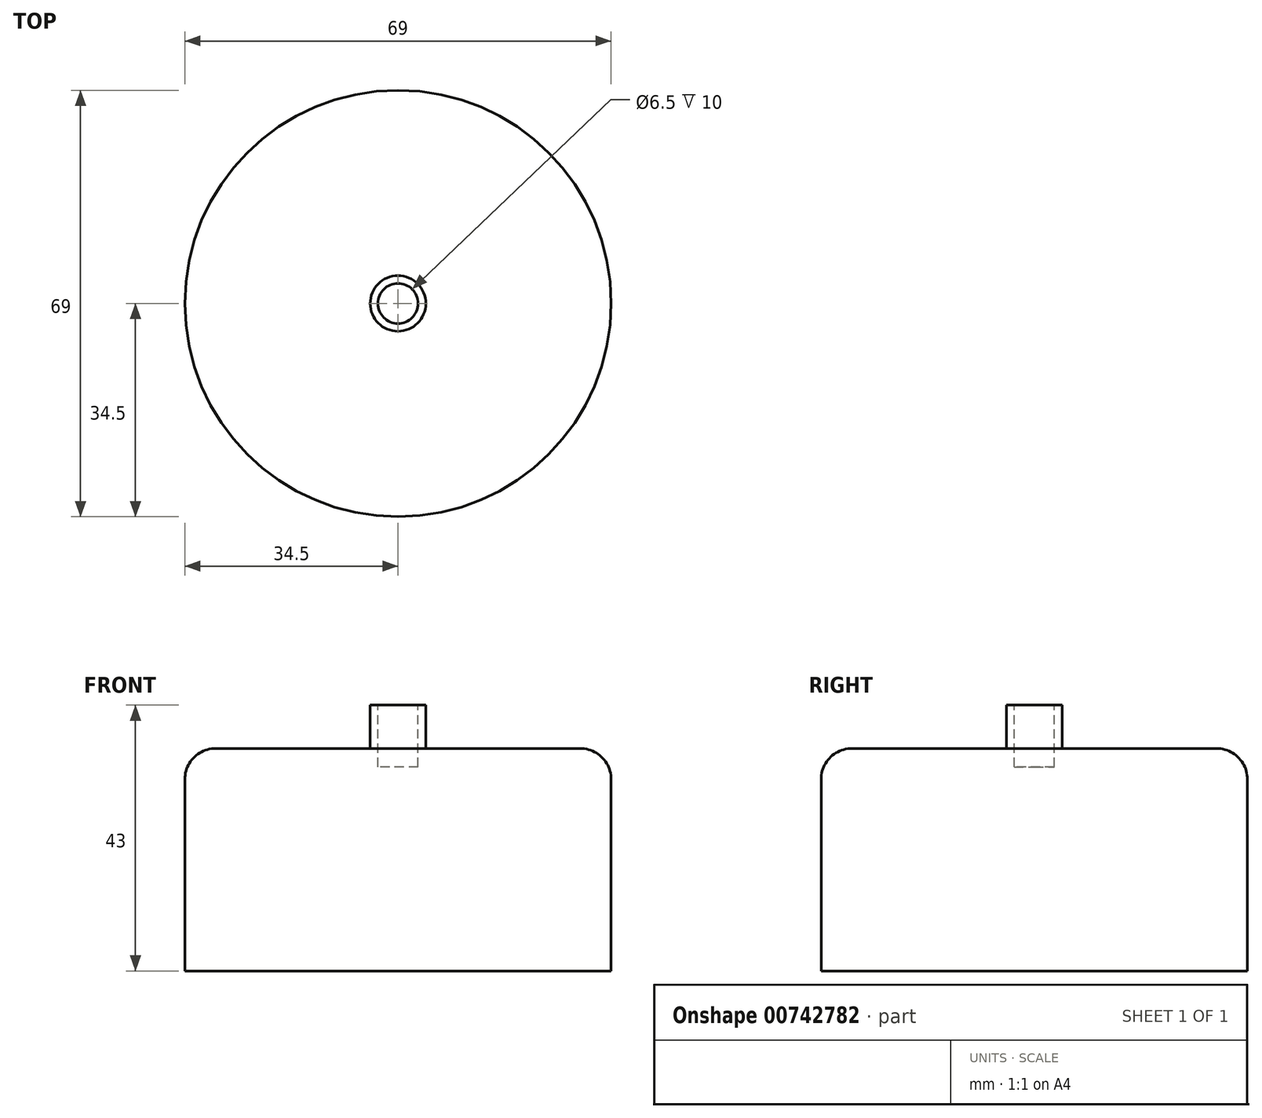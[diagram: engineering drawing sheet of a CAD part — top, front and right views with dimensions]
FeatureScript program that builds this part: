
annotation { "Feature Type Name" : "Feature", "Feature Type Description" : "" }
export const myFeature = defineFeature(function(context is Context, id is Id, definition is map)
    precondition{}
    {
        {
            var Q0;
            Q0=qCreatedBy(makeId("Top.planeOp"),FACE);
            var sketch = newSketch(context, id + "F0", { "sketchPlane" : qUnion([Q0])});
            skCircle(sketch, "E0", {"center": v(0, 0) * mm, "radius": 34.5 * mm});
            skSolve(sketch);
        }
        {
            var Q0;
            Q0=qCreatedBy(makeId("Top.planeOp"),FACE);
            var sketch = newSketch(context, id + "F1", { "sketchPlane" : qUnion([Q0])});
            skCircle(sketch, "E1", {"center": v(0, 0) * mm, "radius": 3.25 * mm});
            skSolve(sketch);
        }
        {
            var Q0;
            Q0=qCreatedBy(makeId("Top.planeOp"),FACE);
            var sketch = newSketch(context, id + "F2", { "sketchPlane" : qUnion([Q0])});
            skCircle(sketch, "E2", {"center": v(0, 0) * mm, "radius": 4.5 * mm});
            skSolve(sketch);
        }
        {
            var Q0;
            Q0=qSketchRegion(id+"F1",true);
            extrude(context, id + "F3", {"entities" : qUnion([Q0]), "depth" : 10 * mm, "offsetDistance" : 25 * mm});
        }
        {
            var Q0;
            Q0=makeQuery(id+"F0.imprint","IMPRINT",FACE,{"disambiguationData":[TD([[makeQuery(id+"F0.imprint","IMPRINT",EDGE,{"derivedFrom":sQuery(id+"F0.wireOp",EDGE,"E0")}),1.0]])]});
            extrude(context, id + "F4", {"entities" : qUnion([Q0]), "operationType" : NewBodyOperationType.ADD, "depth" : 36 * mm, "offsetDistance" : 25 * mm});
        }
        {
            var Q0;
            Q0=qSketchRegion(id+"F2",true);
            extrude(context, id + "F5", {"entities" : qUnion([Q0]), "operationType" : NewBodyOperationType.ADD, "depth" : 43 * mm, "offsetDistance" : 25 * mm});
        }
        {
            var Q0;
            Q0=makeQuery(id+"F4.opExtrude","CAP_EDGE",EDGE,{"disambiguationData":[OSD([sQuery(id+"F0.wireOp",EDGE,"E0")])],"isStart":false});
            fillet(context, id + "F6", {"entities" : qUnion([Q0]), "radius" : 5 * mm, "tangentPropagation" : true, "allowEdgeOverflow" : false});
        }
        {
            var Q0;
            Q0=makeQuery(id+"F5.opExtrude","CAP_FACE",FACE,{"disambiguationData":[OSD([sQuery(id+"F2.wireOp",EDGE,"E2")])],"isStart":false});
            var sketch = newSketch(context, id + "F7", { "sketchPlane" : qUnion([Q0])});
            skCircle(sketch, "E3", {"center": v(0, 0) * mm, "radius": 3.25 * mm});
            skSolve(sketch);
        }
        {
            var Q0;
            Q0 = qSketchRegion(id + "F7", true);
            extrude(context, id + "F8", {"entities" : qUnion([Q0]), "operationType" : NewBodyOperationType.REMOVE, "oppositeDirection" : true, "depth" : 10 * mm, "offsetDistance" : 25 * mm});
        }
    });
